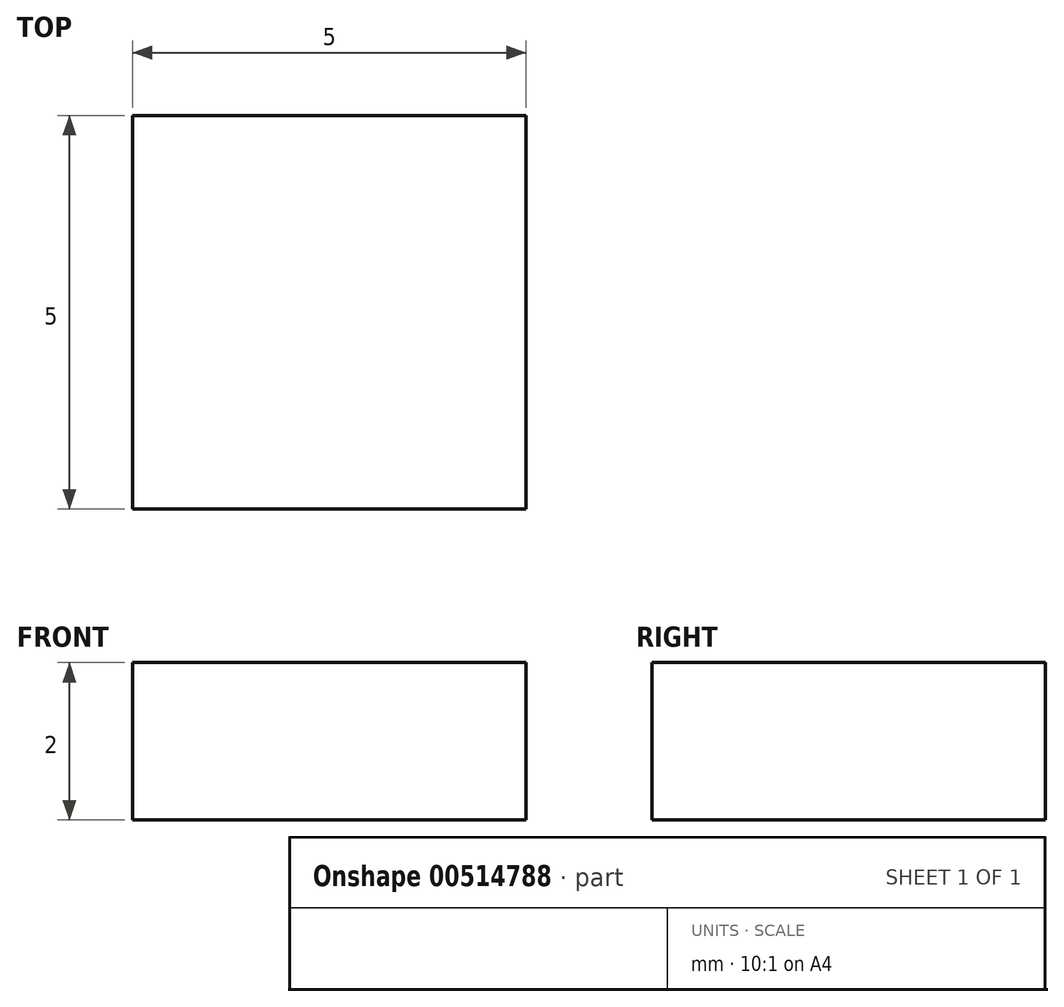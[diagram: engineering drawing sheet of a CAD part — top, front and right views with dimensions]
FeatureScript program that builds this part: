
annotation { "Feature Type Name" : "Feature", "Feature Type Description" : "" }
export const myFeature = defineFeature(function(context is Context, id is Id, definition is map)
    precondition{}
    {
        {
            var Q0;
            Q0=qCreatedBy(makeId("Top.planeOp"),FACE);
            var sketch = newSketch(context, id + "F0", { "sketchPlane" : qUnion([Q0])});
            skLineSegment(sketch, "E0.bottom", {"start": v(2.5, 2.5) * mm, "end": v(-2.5, 2.5) * mm});
            skLineSegment(sketch, "E0.top", {"start": v(2.5, -2.5) * mm, "end": v(-2.5, -2.5) * mm});
            skLineSegment(sketch, "E0.left", {"start": v(2.5, 2.5) * mm, "end": v(2.5, -2.5) * mm});
            skLineSegment(sketch, "E0.right", {"start": v(-2.5, 2.5) * mm, "end": v(-2.5, -2.5) * mm});
            skPoint(sketch, "E0.middle", {"position": v(0, 0) * mm});
            skSolve(sketch);
        }
        {
            var Q0;
            Q0 = qSketchRegion(id + "F0", true);
            extrude(context, id + "F1", {"entities" : qUnion([Q0]), "depth" : 2 * mm, "offsetDistance" : 25.4 * mm});
        }
    });
